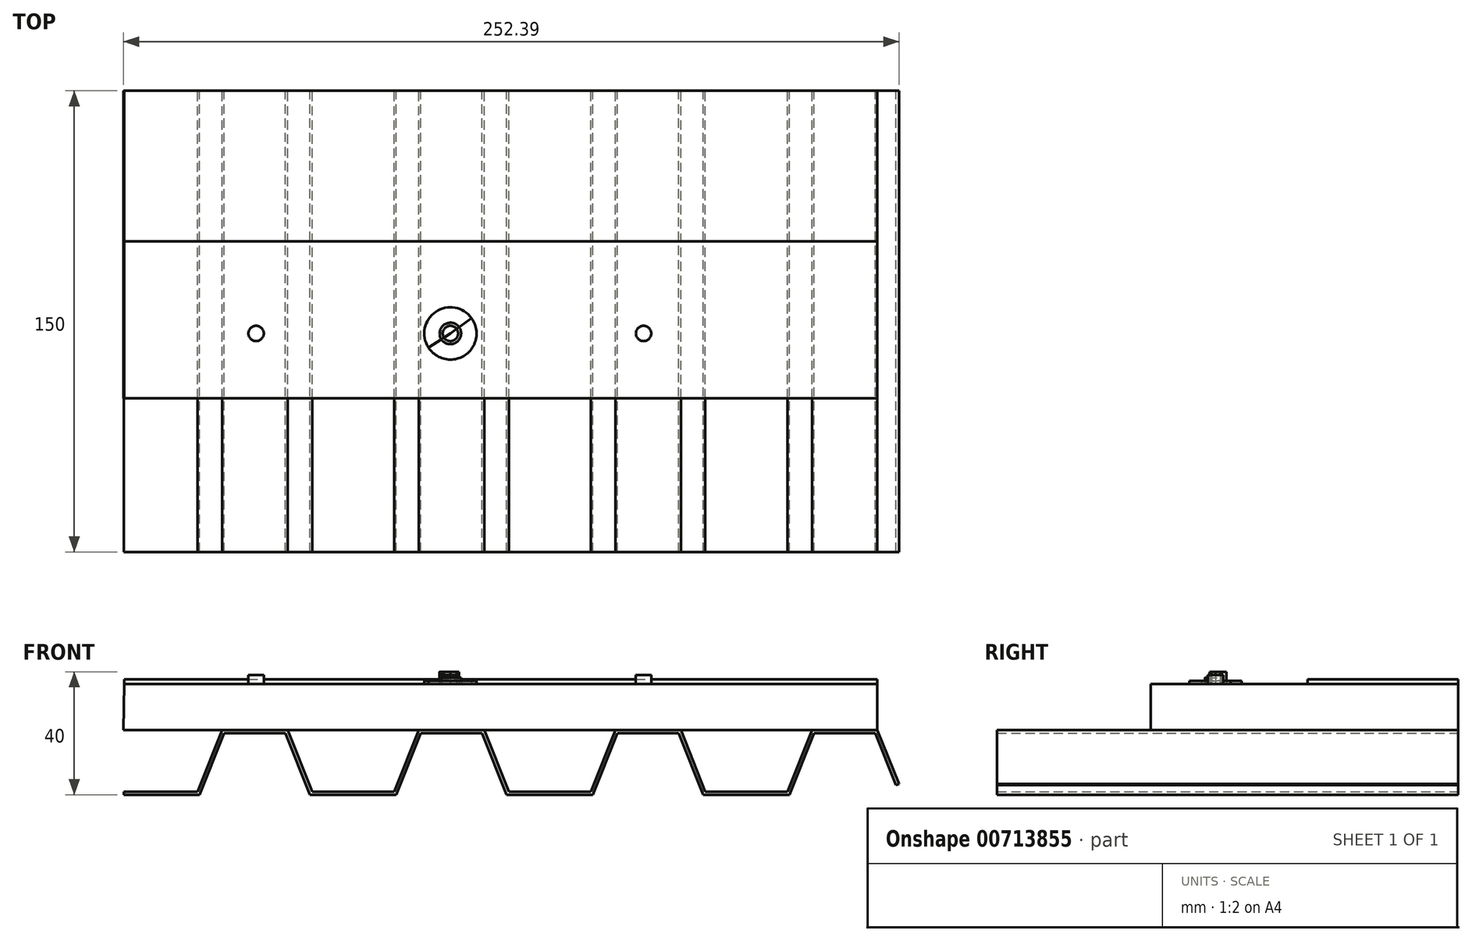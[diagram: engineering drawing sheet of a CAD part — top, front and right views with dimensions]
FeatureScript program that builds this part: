
annotation { "Feature Type Name" : "Feature", "Feature Type Description" : "" }
export const myFeature = defineFeature(function(context is Context, id is Id, definition is map)
    precondition{}
    {
        {
            var Q0;
            Q0=qCreatedBy(makeId("Front.planeOp"),FACE);
            var sketch = newSketch(context, id + "F0", { "sketchPlane" : qUnion([Q0])});
            skLineSegment(sketch, "E0", {"start": v(-75.05, -4) * mm, "end": v(-51.05, -4) * mm});
            skLineSegment(sketch, "E1", {"start": v(-51.05, -4) * mm, "end": v(-43.05, 16) * mm});
            skLineSegment(sketch, "E2", {"start": v(-43.05, 16) * mm, "end": v(-21.76, 16) * mm});
            skLineSegment(sketch, "E3", {"start": v(-21.76, 16) * mm, "end": v(-13.76, -4) * mm});
            skLineSegment(sketch, "E4", {"start": v(-13.76, -4) * mm, "end": v(12.95, -4) * mm});
            skLineSegment(sketch, "E5", {"start": v(12.95, -4) * mm, "end": v(20.95, 16) * mm});
            skLineSegment(sketch, "E6", {"start": v(20.95, 16) * mm, "end": v(42.24, 16) * mm});
            skLineSegment(sketch, "E7", {"start": v(42.24, 16) * mm, "end": v(50.24, -4) * mm});
            skLineSegment(sketch, "E8", {"start": v(50.24, -4) * mm, "end": v(76.95, -4) * mm});
            skLineSegment(sketch, "E9", {"start": v(76.95, -4) * mm, "end": v(84.95, 16) * mm});
            skLineSegment(sketch, "E10", {"start": v(84.95, 16) * mm, "end": v(106.24, 16) * mm});
            skLineSegment(sketch, "E11", {"start": v(106.24, 16) * mm, "end": v(114.24, -4) * mm});
            skLineSegment(sketch, "E12", {"start": v(114.24, -4) * mm, "end": v(140.95, -4) * mm});
            skLineSegment(sketch, "E13", {"start": v(140.95, -4) * mm, "end": v(148.95, 16) * mm});
            skLineSegment(sketch, "E14", {"start": v(148.95, 16) * mm, "end": v(170.24, 16) * mm});
            skLineSegment(sketch, "E15", {"start": v(170.24, 16) * mm, "end": v(177.23, -1.49) * mm});
            skLineSegment(sketch, "E16.0", {"start": v(169.56, 15) * mm, "end": v(176.3, -1.86) * mm});
            skLineSegment(sketch, "E16.1", {"start": v(149.62, 15) * mm, "end": v(169.56, 15) * mm});
            skLineSegment(sketch, "E16.2", {"start": v(141.62, -5) * mm, "end": v(149.62, 15) * mm});
            skLineSegment(sketch, "E16.3", {"start": v(113.56, -5) * mm, "end": v(141.62, -5) * mm});
            skLineSegment(sketch, "E16.4", {"start": v(105.56, 15) * mm, "end": v(113.56, -5) * mm});
            skLineSegment(sketch, "E16.5", {"start": v(85.62, 15) * mm, "end": v(105.56, 15) * mm});
            skLineSegment(sketch, "E16.6", {"start": v(-22.44, 15) * mm, "end": v(-14.44, -5) * mm});
            skLineSegment(sketch, "E16.7", {"start": v(-42.38, 15) * mm, "end": v(-22.44, 15) * mm});
            skLineSegment(sketch, "E16.8", {"start": v(-50.38, -5) * mm, "end": v(-42.38, 15) * mm});
            skLineSegment(sketch, "E16.9", {"start": v(-75.05, -5) * mm, "end": v(-50.38, -5) * mm});
            skLineSegment(sketch, "E16.10", {"start": v(-14.44, -5) * mm, "end": v(13.62, -5) * mm});
            skLineSegment(sketch, "E16.11", {"start": v(13.62, -5) * mm, "end": v(21.62, 15) * mm});
            skLineSegment(sketch, "E16.12", {"start": v(21.62, 15) * mm, "end": v(41.56, 15) * mm});
            skLineSegment(sketch, "E16.13", {"start": v(41.56, 15) * mm, "end": v(49.56, -5) * mm});
            skLineSegment(sketch, "E16.14", {"start": v(49.56, -5) * mm, "end": v(77.62, -5) * mm});
            skLineSegment(sketch, "E16.15", {"start": v(77.62, -5) * mm, "end": v(85.62, 15) * mm});
            skLineSegment(sketch, "E17", {"start": v(-75.05, -4) * mm, "end": v(-75.05, -5) * mm});
            skLineSegment(sketch, "E18", {"start": v(177.23, -1.49) * mm, "end": v(176.3, -1.86) * mm});
            skLineSegment(sketch, "E19", {"start": v(-43.05, 16) * mm, "end": v(-80.96, 16) * mm, "construction": true});
            skLineSegment(sketch, "E20", {"start": v(-43.05, 16) * mm, "end": v(188.18, 16) * mm, "construction": true});
            skLineSegment(sketch, "E21", {"start": v(-75.16, 16) * mm, "end": v(170.24, 16) * mm});
            skLineSegment(sketch, "E22", {"start": v(170.24, 31) * mm, "end": v(-74.91, 31) * mm});
            skLineSegment(sketch, "E23", {"start": v(-74.91, 31) * mm, "end": v(-75.16, 16) * mm});
            skLineSegment(sketch, "E24", {"start": v(170.24, 31) * mm, "end": v(170.24, 16) * mm});
            skLineSegment(sketch, "E25", {"start": v(113.56, -5) * mm, "end": v(188.18, -5) * mm, "construction": true});
            skLineSegment(sketch, "E26", {"start": v(188.18, -5) * mm, "end": v(188.18, 16) * mm, "construction": true});
            skLineSegment(sketch, "E27", {"start": v(-74.91, 31) * mm, "end": v(-74.91, 32.5) * mm});
            skLineSegment(sketch, "E28", {"start": v(-74.91, 32.5) * mm, "end": v(170.2, 32.5) * mm});
            skLineSegment(sketch, "E29", {"start": v(170.2, 32.5) * mm, "end": v(170.24, 31) * mm});
            skSolve(sketch);
        }
        {
            var Q0;
            Q0=makeQuery(id+"F0.imprint","IMPRINT",FACE,{"disambiguationData":[TD([[makeQuery(id+"F0.imprint","IMPRINT",EDGE,{"derivedFrom":sQuery(id+"F0.wireOp",EDGE,"E0")}),-1.0]])]});
            extrude(context, id + "F1", {"entities" : qUnion([Q0]), "depth" : 150 * mm});
        }
        {
            var Q0;
            Q0=makeQuery(id+"F0.imprint","IMPRINT",FACE,{"disambiguationData":[TD([[makeQuery(id+"F0.imprint","IMPRINT",EDGE,{"derivedFrom":sQuery(id+"F0.wireOp",EDGE,"E22")}),1.0]])]});
            extrude(context, id + "F2", {"entities" : qUnion([Q0]), "depth" : 100 * mm});
        }
        {
            var Q0;
            Q0=makeQuery(id+"F0.imprint","IMPRINT",FACE,{"disambiguationData":[TD([[makeQuery(id+"F0.imprint","IMPRINT",EDGE,{"derivedFrom":sQuery(id+"F0.wireOp",EDGE,"E22")}),-1.0]])]});
            extrude(context, id + "F3", {"entities" : qUnion([Q0]), "depth" : 49 * mm});
        }
        {
            var Q0;
            Q0=makeQuery(id+"F2.opExtrude","SWEPT_FACE",FACE,{"disambiguationData":[OSD([sQuery(id+"F0.wireOp",EDGE,"E22")])]});
            var sketch = newSketch(context, id + "F4", { "sketchPlane" : qUnion([Q0])});
            skCircle(sketch, "E30", {"center": v(-32, -78.93) * mm, "radius": 2.5 * mm});
            skCircle(sketch, "E31", {"center": v(31.24, -78.93) * mm, "radius": 2.5 * mm});
            skCircle(sketch, "E32", {"center": v(94.13, -78.93) * mm, "radius": 2.5 * mm});
            skCircle(sketch, "E33.0", {"center": v(31.24, -78.93) * mm, "radius": 3.5 * mm});
            skCircle(sketch, "E34.0", {"center": v(31.24, -78.93) * mm, "radius": 8.5 * mm});
            skLineSegment(sketch, "E35", {"start": v(31.24, -78.93) * mm, "end": v(29.17, -80.32) * mm});
            skLineSegment(sketch, "E36", {"start": v(29.17, -80.32) * mm, "end": v(28.35, -80.9) * mm});
            skLineSegment(sketch, "E37", {"start": v(28.35, -80.9) * mm, "end": v(24.08, -83.5) * mm});
            skLineSegment(sketch, "E38", {"start": v(24.08, -83.5) * mm, "end": v(31.24, -78.93) * mm});
            skLineSegment(sketch, "E39", {"start": v(33.27, -77.47) * mm, "end": v(31.24, -78.93) * mm});
            skLineSegment(sketch, "E40", {"start": v(33.27, -77.47) * mm, "end": v(34.06, -76.86) * mm});
            skLineSegment(sketch, "E41", {"start": v(34.06, -76.86) * mm, "end": v(38.14, -73.96) * mm});
            skSolve(sketch);
        }
        {
            var Q0;
            Q0=makeQuery(id+"F4.imprint","IMPRINT",FACE,{"disambiguationData":[TD([[makeQuery(id+"F4.imprint","IMPRINT",EDGE,{"derivedFrom":sQuery(id+"F4.wireOp",EDGE,"E32")}),1.0]])]});
            extrude(context, id + "F5", {"entities" : qUnion([Q0]), "depth" : 3 * mm});
        }
        {
            var Q0;
            Q0=makeQuery(id+"F4.imprint","IMPRINT",FACE,{"disambiguationData":[TD([[makeQuery(id+"F4.imprint","IMPRINT",EDGE,{"derivedFrom":sQuery(id+"F4.wireOp",EDGE,"E30")}),1.0]])]});
            extrude(context, id + "F6", {"entities" : qUnion([Q0]), "depth" : 3 * mm});
        }
        {
            var Q0;
            {var subQ0=sQuery(id+"F4.wireOp",EDGE,"E35");Q0=makeQuery(id+"F4.imprint","IMPRINT",FACE,{"disambiguationData":[TD([[makeQuery(id+"F4.imprint","IMPRINT",EDGE,{"derivedFrom":subQ0}),1.0]])]});}
            extrude(context, id + "F7", {"entities" : qUnion([Q0]), "depth" : 3 * mm});
        }
        {
            var Q0;
            {var subQ0=sQuery(id+"F4.wireOp",EDGE,"E39");Q0=makeQuery(id+"F4.imprint","IMPRINT",FACE,{"disambiguationData":[TD([[makeQuery(id+"F4.imprint","IMPRINT",EDGE,{"derivedFrom":subQ0}),-1.0]])]});}
            extrude(context, id + "F8", {"entities" : qUnion([Q0]), "depth" : 4 * mm});
        }
        {
            var Q0;
            {var subQ0=sQuery(id+"F4.wireOp",EDGE,"E40");Q0=makeQuery(id+"F4.imprint","IMPRINT",FACE,{"disambiguationData":[TD([[makeQuery(id+"F4.imprint","IMPRINT",EDGE,{"derivedFrom":subQ0}),1.0]])]});}
            extrude(context, id + "F9", {"entities" : qUnion([Q0]), "depth" : 4 * mm});
        }
        {
            var Q0;
            {var subQ0=sQuery(id+"F4.wireOp",EDGE,"E36");Q0=makeQuery(id+"F4.imprint","IMPRINT",FACE,{"disambiguationData":[TD([[makeQuery(id+"F4.imprint","IMPRINT",EDGE,{"derivedFrom":subQ0}),1.0]])]});}
            extrude(context, id + "F10", {"entities" : qUnion([Q0]), "depth" : 2 * mm});
        }
        {
            var Q0;
            {var subQ0=sQuery(id+"F4.wireOp",EDGE,"E41");Q0=makeQuery(id+"F4.imprint","IMPRINT",FACE,{"disambiguationData":[TD([[makeQuery(id+"F4.imprint","IMPRINT",EDGE,{"derivedFrom":subQ0}),1.0]])]});}
            extrude(context, id + "F11", {"entities" : qUnion([Q0]), "depth" : 1 * mm});
        }
        {
            var Q0;
            {var subQ0=sQuery(id+"F4.wireOp",EDGE,"E37");Q0=makeQuery(id+"F4.imprint","IMPRINT",FACE,{"disambiguationData":[TD([[makeQuery(id+"F4.imprint","IMPRINT",EDGE,{"derivedFrom":subQ0}),1.0]])]});}
            extrude(context, id + "F12", {"entities" : qUnion([Q0]), "depth" : 1 * mm});
        }
    });
